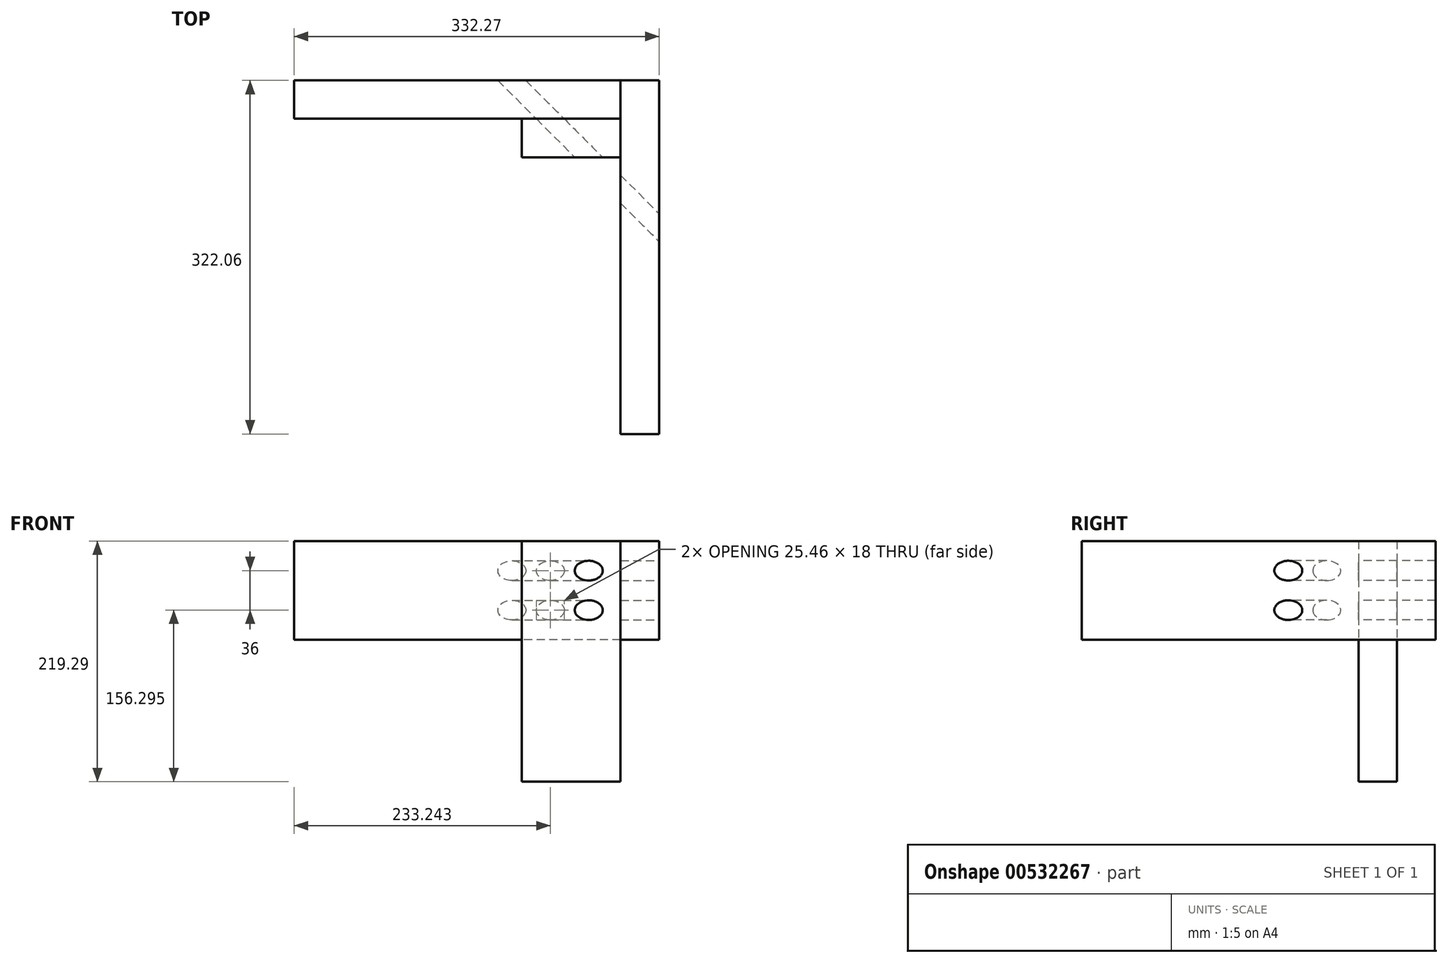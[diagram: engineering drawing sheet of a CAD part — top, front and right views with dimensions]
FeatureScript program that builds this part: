
annotation { "Feature Type Name" : "Feature", "Feature Type Description" : "" }
export const myFeature = defineFeature(function(context is Context, id is Id, definition is map)
    precondition{}
    {
        {
            var Q0;
            Q0=qCreatedBy(makeId("Front.planeOp"),FACE);
            var sketch = newSketch(context, id + "F0", { "sketchPlane" : qUnion([Q0])});
            skLineSegment(sketch, "E0.bottom", {"start": v(-39.17, 14.96) * mm, "end": v(50.83, 14.96) * mm});
            skLineSegment(sketch, "E0.top", {"start": v(-39.17, -204.33) * mm, "end": v(50.83, -204.33) * mm});
            skLineSegment(sketch, "E0.left", {"start": v(-39.17, 14.96) * mm, "end": v(-39.17, -204.33) * mm});
            skLineSegment(sketch, "E0.right", {"start": v(50.83, 14.96) * mm, "end": v(50.83, -204.33) * mm});
            skSolve(sketch);
        }
        {
            var Q0;
            Q0=makeQuery(id+"F0.imprint","IMPRINT",FACE,{"disambiguationData":[TD([[makeQuery(id+"F0.imprint","IMPRINT",EDGE,{"derivedFrom":sQuery(id+"F0.wireOp",EDGE,"E0.bottom")}),-1.0]])]});
            extrude(context, id + "F1", {"entities" : qUnion([Q0]), "depth" : 35 * mm, "offsetDistance" : 25 * mm});
        }
        {
            var Q0;
            Q0=makeQuery(id+"F1.opExtrude","CAP_FACE",FACE,{"disambiguationData":[OSD([sQuery(id+"F0.wireOp",EDGE,"E0.bottom"),sQuery(id+"F0.wireOp",EDGE,"E0.top"),sQuery(id+"F0.wireOp",EDGE,"E0.left"),sQuery(id+"F0.wireOp",EDGE,"E0.right")])],"isStart":true});
            var sketch = newSketch(context, id + "F2", { "sketchPlane" : qUnion([Q0])});
            skLineSegment(sketch, "E1.bottom", {"start": v(-50.83, 14.96) * mm, "end": v(246.44, 14.96) * mm});
            skLineSegment(sketch, "E1.top", {"start": v(-50.83, -75.04) * mm, "end": v(246.44, -75.04) * mm});
            skLineSegment(sketch, "E1.left", {"start": v(-50.83, 14.96) * mm, "end": v(-50.83, -75.04) * mm});
            skLineSegment(sketch, "E1.right", {"start": v(246.44, 14.96) * mm, "end": v(246.44, -75.04) * mm});
            skSolve(sketch);
        }
        {
            var Q0;
            {var subQ3=sQuery(id+"F2.wireOp",EDGE,"E1.right");Q0=makeQuery(id+"F2.imprint","IMPRINT",FACE,{"disambiguationData":[TD([[makeQuery(id+"F2.imprint","IMPRINT",EDGE,{"derivedFrom":subQ3}),-1.0]])]});}
            var Q1;
            {var subQ3=sQuery(id+"F2.wireOp",EDGE,"E1.left");Q1=makeQuery(id+"F2.imprint","IMPRINT",FACE,{"disambiguationData":[TD([[makeQuery(id+"F2.imprint","IMPRINT",EDGE,{"derivedFrom":subQ3}),1.0]])]});}
            extrude(context, id + "F3", {"entities" : qUnion([Q0, Q1]), "depth" : 35 * mm, "offsetDistance" : 25 * mm});
        }
        {
            var Q0;
            Q0=makeQuery(id+"F3.opExtrude","SWEPT_FACE",FACE,{"disambiguationData":[OSD([sQuery(id+"F2.wireOp",EDGE,"E1.left")])]});
            var sketch = newSketch(context, id + "F4", { "sketchPlane" : qUnion([Q0])});
            skLineSegment(sketch, "E2.bottom", {"start": v(35, 14.96) * mm, "end": v(-287.06, 14.96) * mm});
            skLineSegment(sketch, "E2.top", {"start": v(35, -75.04) * mm, "end": v(-287.06, -75.04) * mm});
            skLineSegment(sketch, "E2.left", {"start": v(35, 14.96) * mm, "end": v(35, -75.04) * mm});
            skLineSegment(sketch, "E2.right", {"start": v(-287.06, 14.96) * mm, "end": v(-287.06, -75.04) * mm});
            skSolve(sketch);
        }
        {
            var Q0;
            {var subQ2=sQuery(id+"F4.wireOp",EDGE,"E2.left");Q0=makeQuery(id+"F4.imprint","IMPRINT",FACE,{"disambiguationData":[TD([[makeQuery(id+"F4.imprint","IMPRINT",EDGE,{"derivedFrom":subQ2}),-1.0]])]});}
            var Q1;
            {var subQ2=sQuery(id+"F4.wireOp",EDGE,"E2.right");Q1=makeQuery(id+"F4.imprint","IMPRINT",FACE,{"disambiguationData":[TD([[makeQuery(id+"F4.imprint","IMPRINT",EDGE,{"derivedFrom":subQ2}),1.0]])]});}
            extrude(context, id + "F5", {"entities" : qUnion([Q0, Q1]), "depth" : 35 * mm, "offsetDistance" : 25 * mm});
        }
        {
            var Q0;
            Q0=makeQuery(id+"F3.opExtrude","CAP_FACE",FACE,{"disambiguationData":[OSD([sQuery(id+"F2.wireOp",EDGE,"E1.bottom"),sQuery(id+"F2.wireOp",EDGE,"E1.top"),sQuery(id+"F2.wireOp",EDGE,"E1.left"),sQuery(id+"F2.wireOp",EDGE,"E1.right")])],"isStart":false});
            var sketch = newSketch(context, id + "F6", { "sketchPlane" : qUnion([Q0])});
            skLineSegment(sketch, "E3", {"start": v(48.2, 14.96) * mm, "end": v(48.2, -75.04) * mm, "construction": true});
            skSolve(sketch);
        }
        {
            var Q0;
            Q0=makeQuery(id+"F6.imprint","IMPRINT",FACE,{"disambiguationData":[TD([[makeQuery(id+"F6.imprint","IMPRINT",EDGE,{"derivedFrom":makeQuery(id+"F3.opExtrude","CAP_EDGE",EDGE,{"disambiguationData":[OSD([sQuery(id+"F2.wireOp",EDGE,"E1.bottom")])],"isStart":false})}),-1.0]])]});
            var Q1;
            Q1=sQuery(id+"F6.wireOp",EDGE,"E3");
            cPlane(context, id + "F7", {"entities" : qUnion([Q0, Q1]), "cplaneType" : CPlaneType.LINE_ANGLE, "offset" : 25 * mm, "angle" : 135 * degree, "width" : 150 * mm, "height" : 150 * mm});
        }
        {
            var Q0;
            Q0=qCreatedBy(id+"F7.planeOp",FACE);
            var sketch = newSketch(context, id + "F8", { "sketchPlane" : qUnion([Q0])});
            skCircle(sketch, "E4", {"center": v(9.33, -12.04) * mm, "radius": 9 * mm});
            skCircle(sketch, "E5", {"center": v(9.33, -48.04) * mm, "radius": 9 * mm});
            skLineSegment(sketch, "E6", {"start": v(9.33, -39.04) * mm, "end": v(9.33, -21.04) * mm});
            skPoint(sketch, "E7", {"position": v(9.33, -30.04) * mm});
            skSolve(sketch);
        }
        {
            var Q0;
            Q0=makeQuery(id+"F8.imprint","IMPRINT",FACE,{"disambiguationData":[TD([[makeQuery(id+"F8.imprint","IMPRINT",EDGE,{"derivedFrom":sQuery(id+"F8.wireOp",EDGE,"E4")}),1.0]])]});
            var Q1;
            Q1=makeQuery(id+"F8.imprint","IMPRINT",FACE,{"disambiguationData":[TD([[makeQuery(id+"F8.imprint","IMPRINT",EDGE,{"derivedFrom":sQuery(id+"F8.wireOp",EDGE,"E5")}),1.0]])]});
            extrude(context, id + "F9", {"entities" : qUnion([Q0, Q1]), "operationType" : NewBodyOperationType.REMOVE, "depth" : 25 * mm, "offsetDistance" : 25 * mm, "hasSecondDirection" : true, "secondDirectionOppositeDirection" : true, "secondDirectionDepth" : 205.4 * mm});
        }
    });
